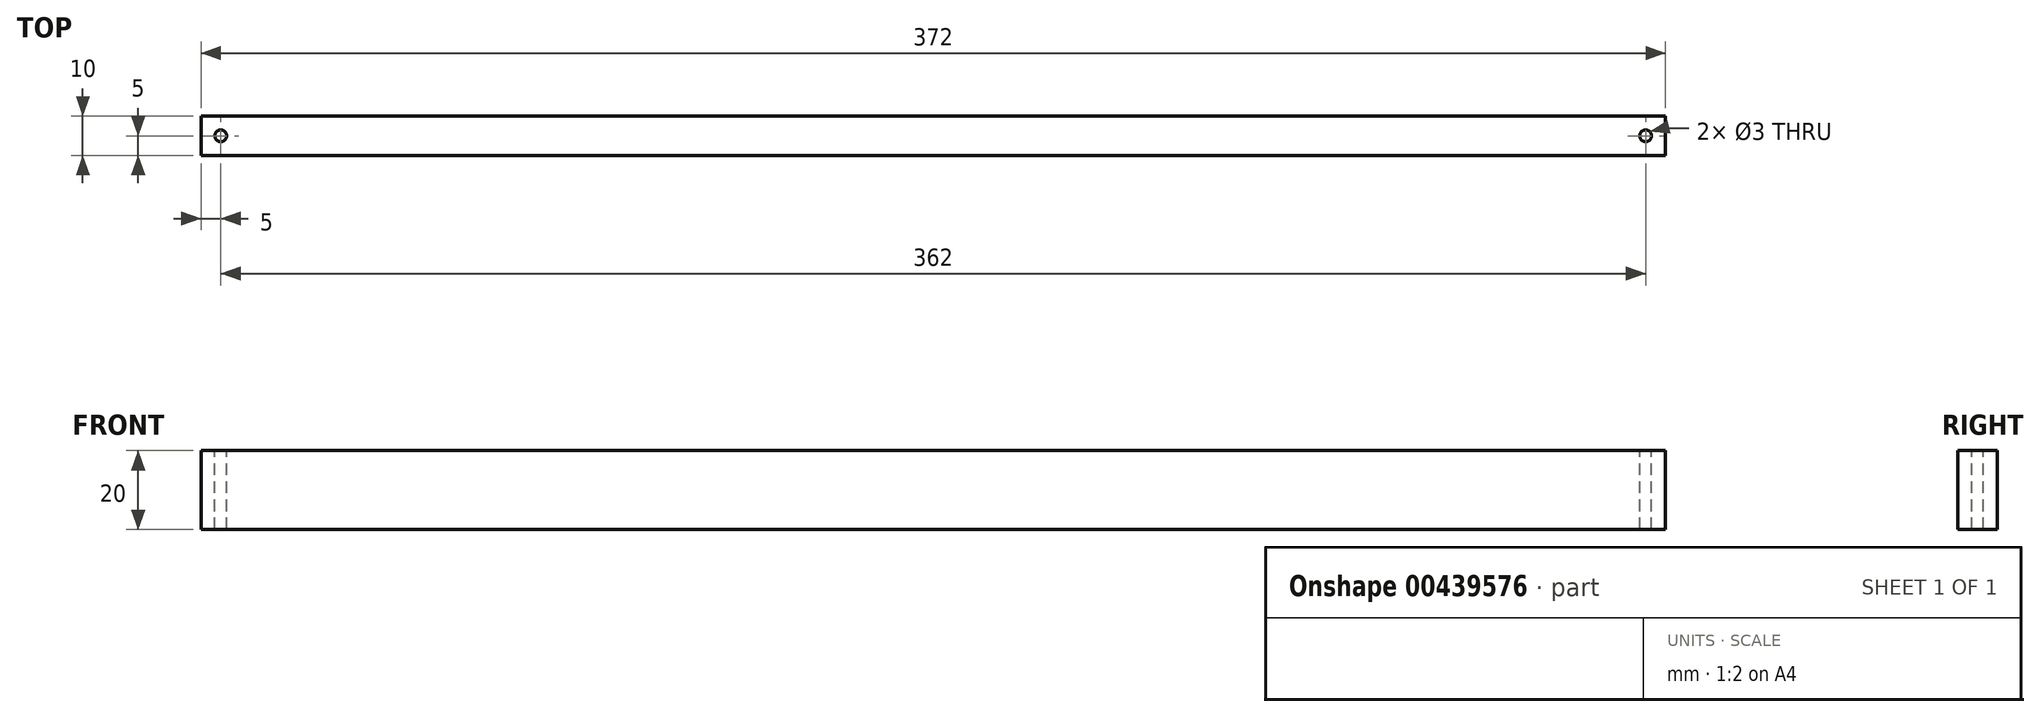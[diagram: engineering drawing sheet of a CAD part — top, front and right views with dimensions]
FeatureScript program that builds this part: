
annotation { "Feature Type Name" : "Feature", "Feature Type Description" : "" }
export const myFeature = defineFeature(function(context is Context, id is Id, definition is map)
    precondition{}
    {
        {
            var Q0;
            Q0=qCreatedBy(makeId("Front.planeOp"),FACE);
            var sketch = newSketch(context, id + "F0", { "sketchPlane" : qUnion([Q0])});
            skLineSegment(sketch, "E0.bottom", {"start": v(-186, -11.36) * mm, "end": v(186, -11.36) * mm});
            skLineSegment(sketch, "E0.top", {"start": v(-186, -31.36) * mm, "end": v(186, -31.36) * mm});
            skLineSegment(sketch, "E0.left", {"start": v(-186, -11.36) * mm, "end": v(-186, -31.36) * mm});
            skLineSegment(sketch, "E0.right", {"start": v(186, -11.36) * mm, "end": v(186, -31.36) * mm});
            skSolve(sketch);
        }
        {
            var Q0;
            Q0 = qSketchRegion(id + "F0", true);
            extrude(context, id + "F1", {"entities" : qUnion([Q0]), "depth" : 10 * mm});
        }
        {
            var Q0;
            Q0=makeQuery(id+"F1.opExtrude","SWEPT_FACE",FACE,{"disambiguationData":[OSD([sQuery(id+"F0.wireOp",EDGE,"E0.bottom")])]});
            var sketch = newSketch(context, id + "F2", { "sketchPlane" : qUnion([Q0])});
            skCircle(sketch, "E1", {"center": v(-181, -5) * mm, "radius": 1.5 * mm});
            skCircle(sketch, "E2", {"center": v(181, -5) * mm, "radius": 1.5 * mm});
            skSolve(sketch);
        }
        {
            var Q0;
            Q0 = qSketchRegion(id + "F2", true);
            extrude(context, id + "F3", {"entities" : qUnion([Q0]), "operationType" : NewBodyOperationType.REMOVE, "endBound" : BoundingType.THROUGH_ALL, "oppositeDirection" : true, "depth" : 25 * mm});
        }
    });
